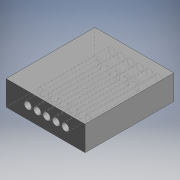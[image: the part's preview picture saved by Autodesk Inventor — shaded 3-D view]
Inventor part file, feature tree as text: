
AUTODESK INVENTOR PART (.ipt)
format: ipt  version: 2019 (Build 230136000, 136)  size: 129,024 bytes
history: native  units: mm (DEFAULTED — no unit token found)
features: sketch x2, hole x2, extrude x1
ambient origin geometry x8: Origin, YZ Plane, XZ Plane, XY Plane, X Axis, Y Axis, Z Axis, Center Point
bodies: Solid1 (feature_tree)
feature tree (5):
  sketch  "Sketch1"  dims[d0=0.0mm d1=57.15mm d2=57.15mm d3=0.0mm]
  sketch  "Sketch2"  dims[d4=4.7625mm d5=19.05mm d6=9.525mm d7=6.35mm d8=14.3117mm d9=45.445274mm d10=20.594885mm d11=4.7625mm d12=19.05mm d13=9.525mm d14=6.35mm d15=14.3117mm d16=45.445274mm d17=20.594885mm]
  extrude  "Extrusion1"  Depth=57.15mm TaperAngle=0.0deg
  hole  "Hole1"  [1 undecoded]
  hole  "Hole2"  [1 undecoded]
note: 2 required parameter values undecoded (feature->parameter linkage not recoverable at this tier; creation-order binding heuristic only, values carry confidence <= 0.55)
